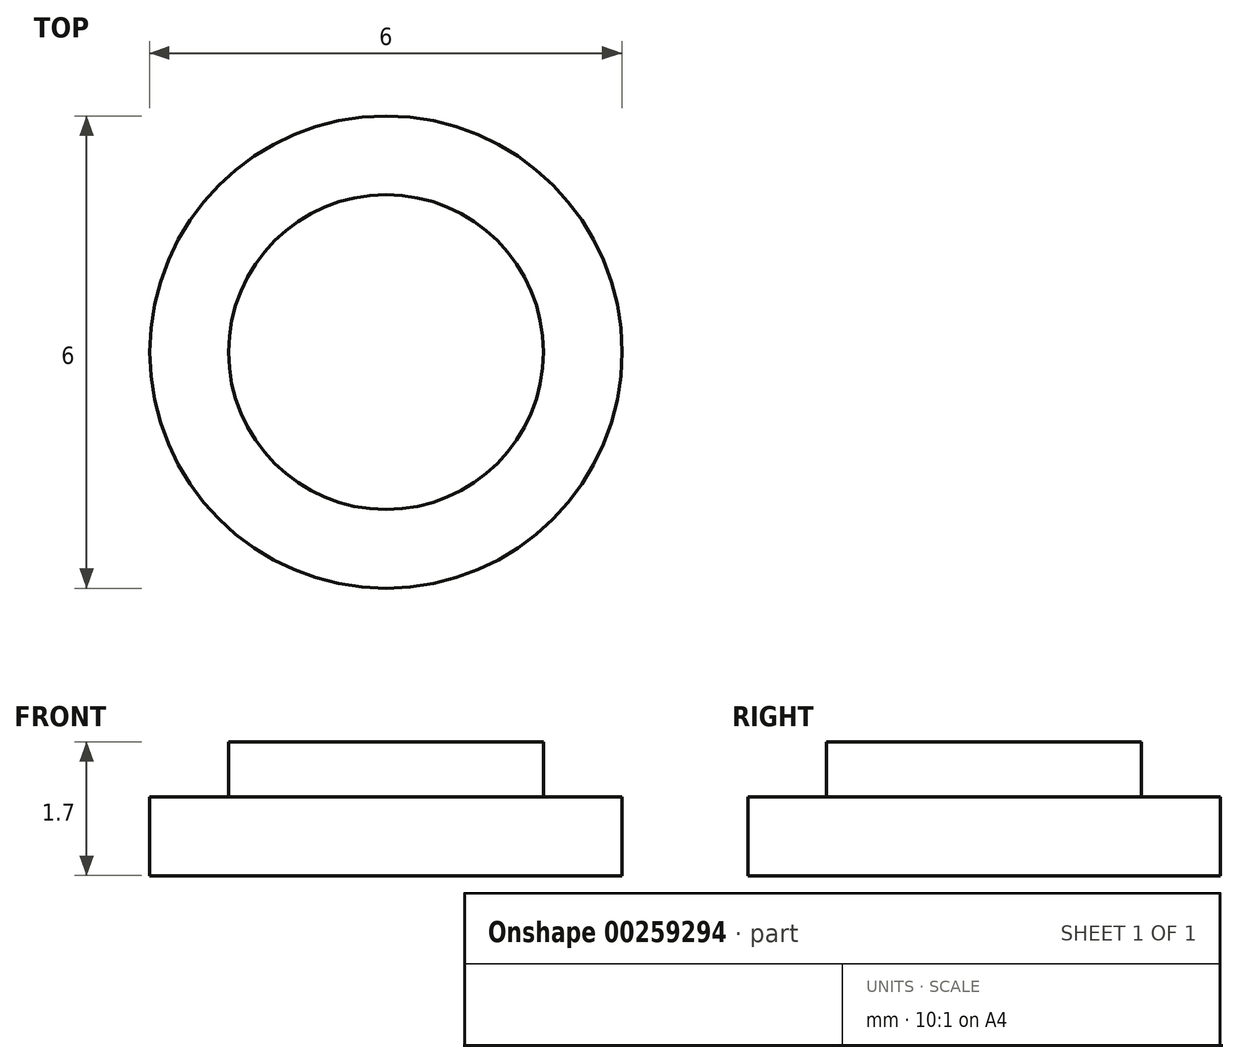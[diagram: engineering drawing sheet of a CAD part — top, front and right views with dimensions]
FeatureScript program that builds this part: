
annotation { "Feature Type Name" : "Feature", "Feature Type Description" : "" }
export const myFeature = defineFeature(function(context is Context, id is Id, definition is map)
    precondition{}
    {
        {
            var Q0;
            Q0=qCreatedBy(makeId("Front.planeOp"),FACE);
            var sketch = newSketch(context, id + "F0", { "sketchPlane" : qUnion([Q0])});
            skLineSegment(sketch, "E0.bottom", {"start": v(-8.05, 24.92) * mm, "end": v(-6.05, 24.92) * mm});
            skLineSegment(sketch, "E0.right", {"start": v(-6.05, 24.92) * mm, "end": v(-6.05, 24.22) * mm});
            skLineSegment(sketch, "E1.top", {"start": v(-5.05, 24.22) * mm, "end": v(-6.05, 24.22) * mm});
            skLineSegment(sketch, "E1.left", {"start": v(-5.05, 23.22) * mm, "end": v(-5.05, 24.22) * mm});
            skLineSegment(sketch, "E2", {"start": v(-8.05, 24.92) * mm, "end": v(-8.05, 23.22) * mm});
            skLineSegment(sketch, "E3", {"start": v(-8.05, 23.22) * mm, "end": v(-5.05, 23.22) * mm});
            skSolve(sketch);
        }
        {
            var Q0;
            Q0 = qSketchRegion(id + "F0", true);
            var Q1;
            Q1=sQuery(id+"F0.wireOp",EDGE,"E2");
            revolve(context, id + "F1", {"entities" : qUnion([Q0]), "axis" : qUnion([Q1]), "revolveType" : RevolveType.FULL});
        }
    });
